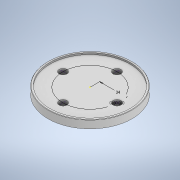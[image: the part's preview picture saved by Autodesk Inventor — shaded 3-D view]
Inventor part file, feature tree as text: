
AUTODESK INVENTOR PART (.ipt)
format: ipt  version: 2021.4 (Build 254397000, 397)  size: 144,896 bytes
history: native  units: mm
features: sketch x4, extrude x3, other x1, hole x1, fillet x1
ambient origin geometry x8: Origin, YZ Plane, XZ Plane, XY Plane, X Axis, Y Axis, Z Axis, Center Point
bodies: Body1 (feature_tree)
feature tree (10):
  other  "ソリッド1"
  extrude  "押し出し1"  Depth=106.0mm
  extrude  "押し出し2"  Depth=10.0mm TaperAngle=0.0deg
  hole  "穴2"  [1 undecoded]
  fillet  "フィレット1"  Radius=2.0mm
  extrude  "押し出し3"  Depth=34.0mm
  sketch  "スケッチ1"
  sketch  "スケッチ2"
  sketch  "スケッチ3"
  sketch  "スケッチ4"
note: 1 required parameter value undecoded (feature->parameter linkage not recoverable at this tier; creation-order binding heuristic only, values carry confidence <= 0.55)
